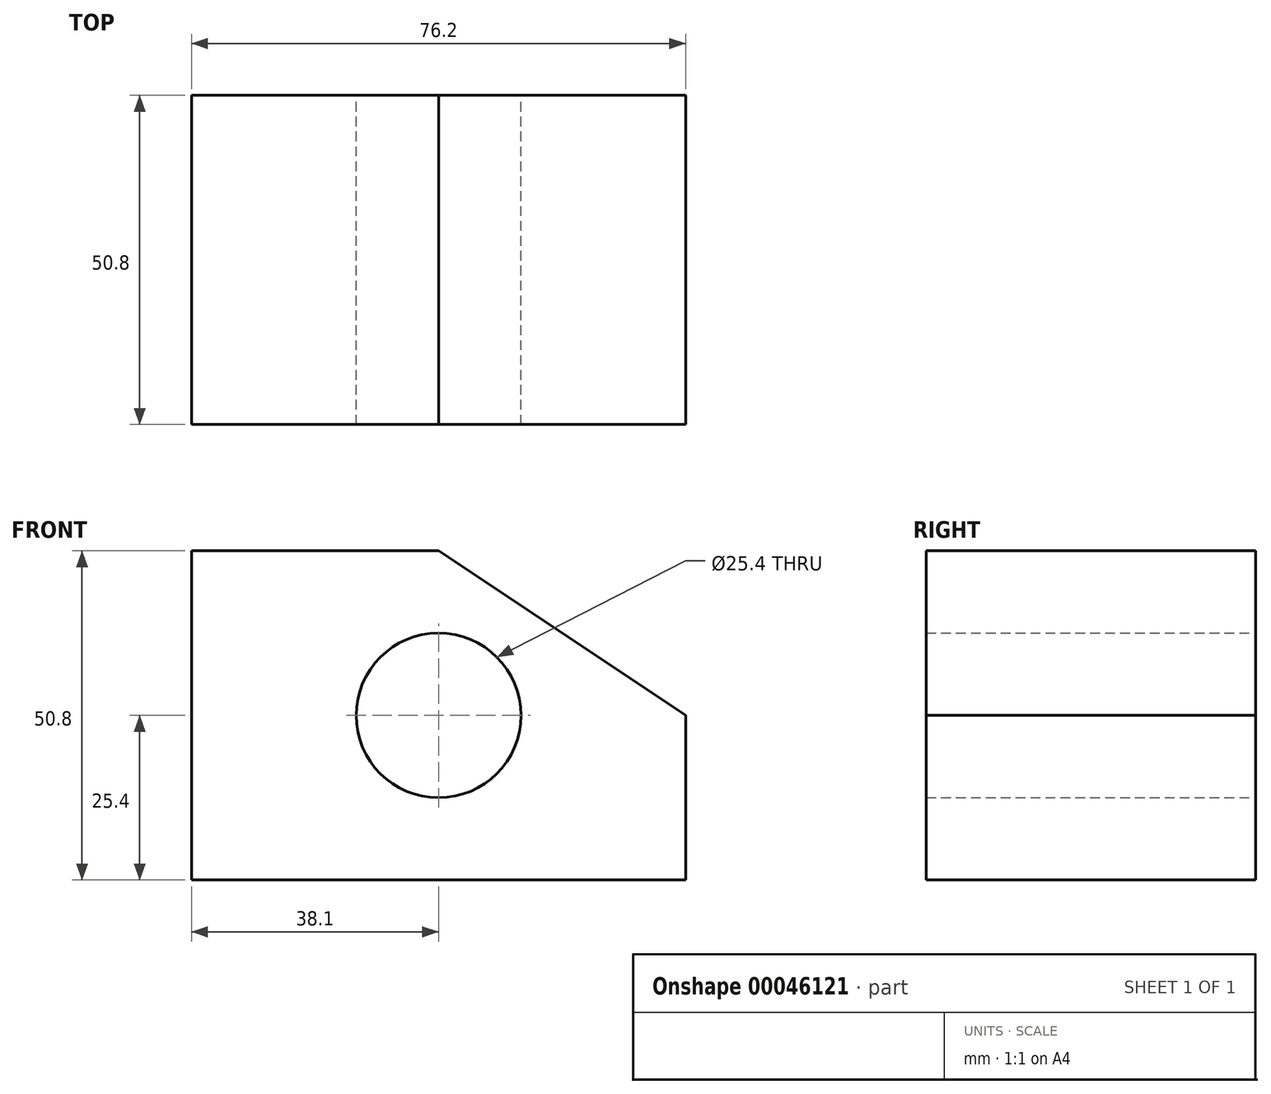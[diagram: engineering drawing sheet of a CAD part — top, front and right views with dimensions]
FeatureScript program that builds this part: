
annotation { "Feature Type Name" : "Feature", "Feature Type Description" : "" }
export const myFeature = defineFeature(function(context is Context, id is Id, definition is map)
    precondition{}
    {
        {
            var Q0;
            Q0=qCreatedBy(makeId("Front.planeOp"),FACE);
            var sketch = newSketch(context, id + "F0", { "sketchPlane" : qUnion([Q0])});
            skLineSegment(sketch, "E0", {"start": v(0, 0) * mm, "end": v(76.2, 0) * mm});
            skLineSegment(sketch, "E1", {"start": v(76.2, 0) * mm, "end": v(76.2, 25.4) * mm});
            skLineSegment(sketch, "E2", {"start": v(76.2, 25.4) * mm, "end": v(38.1, 50.8) * mm});
            skLineSegment(sketch, "E3", {"start": v(38.1, 50.8) * mm, "end": v(0, 50.8) * mm});
            skLineSegment(sketch, "E4", {"start": v(0, 50.8) * mm, "end": v(0, 0) * mm});
            skCircle(sketch, "E5", {"center": v(38.1, 25.4) * mm, "radius": 12.7 * mm});
            skSolve(sketch);
        }
        {
            var Q0;
            Q0=makeQuery(id+"F0.imprint","IMPRINT",FACE,{"disambiguationData":[TD([[makeQuery(id+"F0.imprint","IMPRINT",EDGE,{"derivedFrom":sQuery(id+"F0.wireOp",EDGE,"E0")}),1.0]])]});
            extrude(context, id + "F1", {"entities" : qUnion([Q0]), "endBound" : BoundingType.SYMMETRIC, "depth" : 50.8 * mm});
        }
    });
